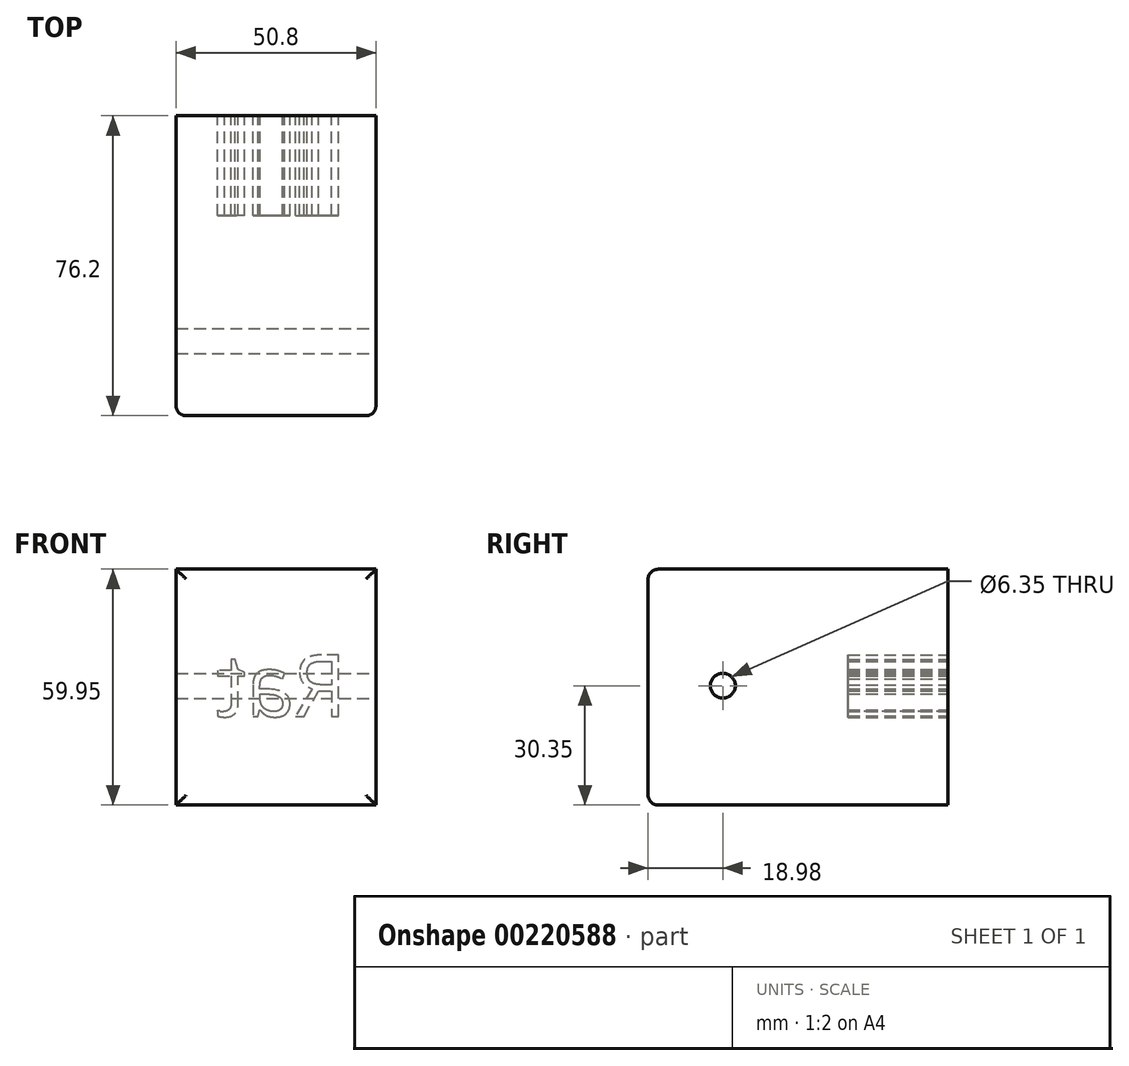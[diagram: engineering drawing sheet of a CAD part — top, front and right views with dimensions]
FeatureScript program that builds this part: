
annotation { "Feature Type Name" : "Feature", "Feature Type Description" : "" }
export const myFeature = defineFeature(function(context is Context, id is Id, definition is map)
    precondition{}
    {
        {
            var Q0;
            Q0=qCreatedBy(makeId("Front.planeOp"),FACE);
            var sketch = newSketch(context, id + "F0", { "sketchPlane" : qUnion([Q0])});
            skLineSegment(sketch, "E0.bottom", {"start": v(-26.22, 39.04) * mm, "end": v(24.58, 39.04) * mm});
            skLineSegment(sketch, "E0.top", {"start": v(-26.22, -20.9) * mm, "end": v(24.58, -20.9) * mm});
            skLineSegment(sketch, "E0.left", {"start": v(-26.22, 39.04) * mm, "end": v(-26.22, -20.9) * mm});
            skLineSegment(sketch, "E0.right", {"start": v(24.58, 39.04) * mm, "end": v(24.58, -20.9) * mm});
            skSolve(sketch);
        }
        {
            var Q0;
            Q0=makeQuery(id+"F0.imprint","IMPRINT",FACE,{"disambiguationData":[TD([[makeQuery(id+"F0.imprint","IMPRINT",EDGE,{"derivedFrom":sQuery(id+"F0.wireOp",EDGE,"E0.bottom")}),-1.0]])]});
            extrude(context, id + "F1", {"entities" : qUnion([Q0]), "depth" : 76.2 * mm});
        }
        {
            var Q0;
            Q0=makeQuery(id+"F1.opExtrude","CAP_FACE",FACE,{"disambiguationData":[OSD([sQuery(id+"F0.wireOp",EDGE,"E0.bottom"),sQuery(id+"F0.wireOp",EDGE,"E0.top"),sQuery(id+"F0.wireOp",EDGE,"E0.left"),sQuery(id+"F0.wireOp",EDGE,"E0.right")])],"isStart":false});
            fillet(context, id + "F2", {"entities" : qUnion([Q0]), "radius" : 2.54 * mm, "tangentPropagation" : true, "allowEdgeOverflow" : false});
        }
        {
            var Q0;
            Q0=makeQuery(id+"F1.opExtrude","SWEPT_FACE",FACE,{"disambiguationData":[OSD([sQuery(id+"F0.wireOp",EDGE,"E0.right")])]});
            var sketch = newSketch(context, id + "F3", { "sketchPlane" : qUnion([Q0])});
            skPoint(sketch, "E1", {"position": v(-57.22, 9.44) * mm});
            skSolve(sketch);
        }
        {
            var Q0;
            Q0=sQuery(id+"F3.wireOp",VERTEX,"E1");
            var Q1;
            Q1=makeQuery(id+"F1.opExtrude","SWEPT_BODY",BODY,{"disambiguationData":[OSD([sQuery(id+"F0.wireOp",EDGE,"E0.bottom"),sQuery(id+"F0.wireOp",EDGE,"E0.top"),sQuery(id+"F0.wireOp",EDGE,"E0.left"),sQuery(id+"F0.wireOp",EDGE,"E0.right")])]});
            hole(context, id + "F4", {"style" : HoleStyle.SIMPLE, "endStyle" : HoleEndStyle.THROUGH, "holeDiameter" : 6.35 * mm, "locations" : qUnion([Q0]), "scope" : qUnion([Q1]), "isTappedThrough" : true});
        }
        {
            var Q0;
            Q0=makeQuery(id+"F1.opExtrude","CAP_FACE",FACE,{"disambiguationData":[OSD([sQuery(id+"F0.wireOp",EDGE,"E0.bottom"),sQuery(id+"F0.wireOp",EDGE,"E0.top"),sQuery(id+"F0.wireOp",EDGE,"E0.left"),sQuery(id+"F0.wireOp",EDGE,"E0.right")])],"isStart":true});
            var sketch = newSketch(context, id + "F5", { "sketchPlane" : qUnion([Q0])});
            skText(sketch, "E2", { "text": "Rat", "fontName": "OpenSans-Regular.ttf"});
            const initialGuessF5  = {"E2": [-0.01723, 0.00164, 1, 0, 0.01574]};
            skSetInitialGuess(sketch, initialGuessF5);
            skSolve(sketch);
        }
        {
            var Q0;
            Q0 = qSketchRegion(id + "F5", true);
            extrude(context, id + "F6", {"entities" : qUnion([Q0]), "operationType" : NewBodyOperationType.REMOVE, "oppositeDirection" : true, "depth" : 25.4 * mm});
        }
    });
